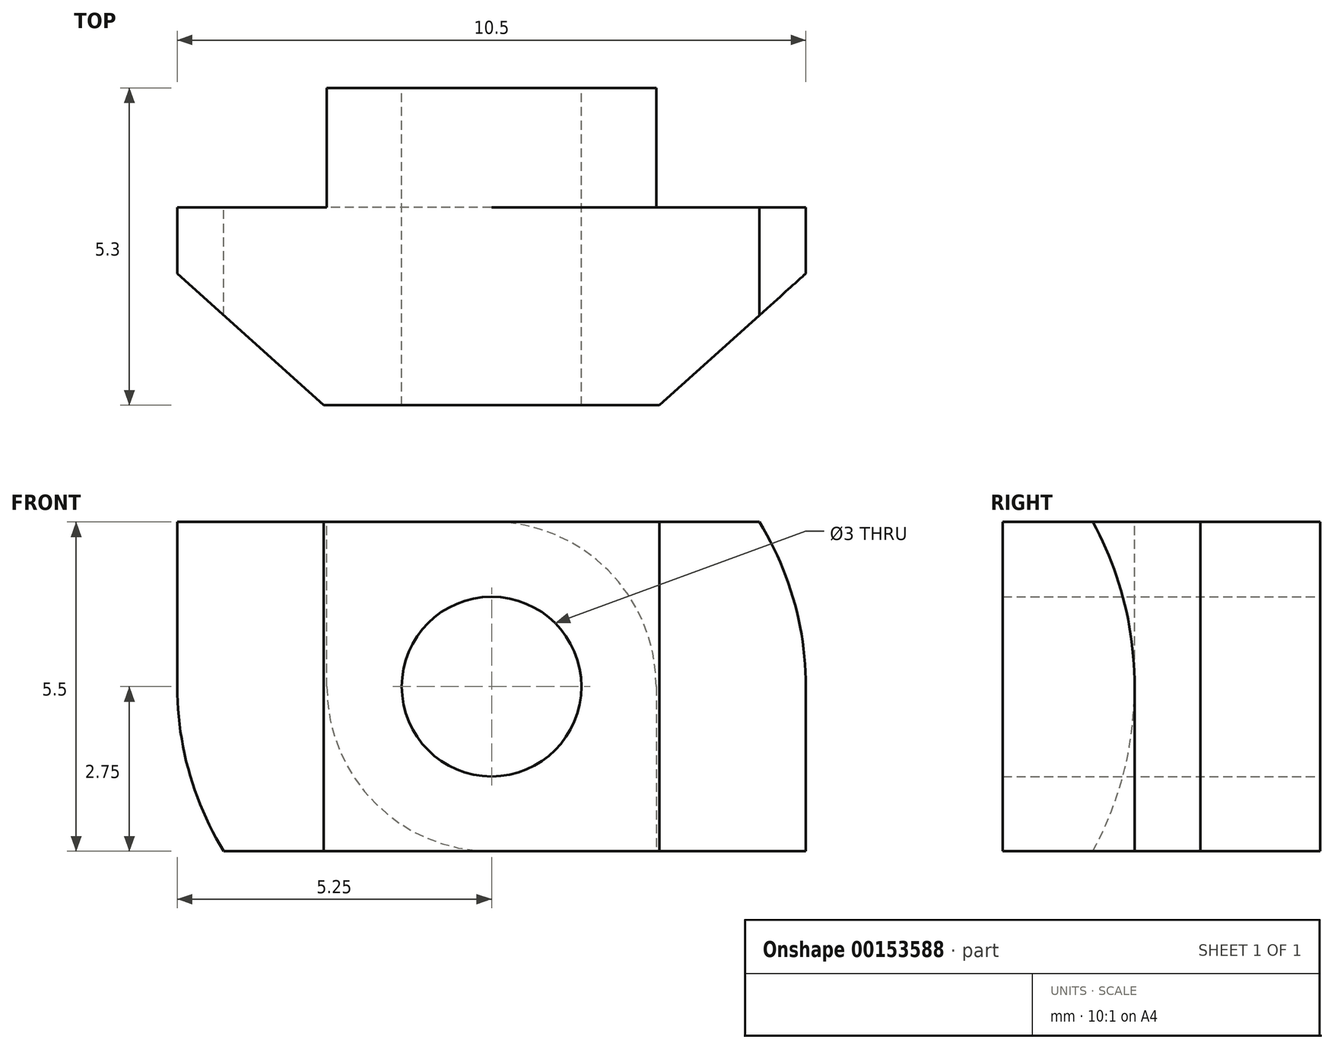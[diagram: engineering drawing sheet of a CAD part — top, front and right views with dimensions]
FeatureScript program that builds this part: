
annotation { "Feature Type Name" : "Feature", "Feature Type Description" : "" }
export const myFeature = defineFeature(function(context is Context, id is Id, definition is map)
    precondition{}
    {
        {
            var Q0;
            Q0=qCreatedBy(makeId("Front.planeOp"),FACE);
            var sketch = newSketch(context, id + "F0", { "sketchPlane" : qUnion([Q0])});
            skLineSegment(sketch, "E0.bottom", {"start": v(5.25, -2.75) * mm, "end": v(-5.25, -2.75) * mm});
            skLineSegment(sketch, "E0.top", {"start": v(5.25, 2.75) * mm, "end": v(-5.25, 2.75) * mm});
            skLineSegment(sketch, "E0.left", {"start": v(5.25, -2.75) * mm, "end": v(5.25, 2.75) * mm});
            skLineSegment(sketch, "E0.right", {"start": v(-5.25, -2.75) * mm, "end": v(-5.25, 2.75) * mm});
            skPoint(sketch, "E0.middle", {"position": v(0, 0) * mm});
            skCircle(sketch, "E1", {"center": v(0, 0) * mm, "radius": 5.25 * mm});
            skCircle(sketch, "E2", {"center": v(0, 0) * mm, "radius": 1.5 * mm});
            skSolve(sketch);
        }
        {
            var Q0;
            Q0=makeQuery(id+"F0.imprint","IMPRINT",FACE,{"disambiguationData":[TD([[makeQuery(id+"F0.imprint","IMPRINT",EDGE,{"derivedFrom":sQuery(id+"F0.wireOp",EDGE,"E2")}),-1.0]])]});
            var Q1;
            {var subQ0=sQuery(id+"F0.wireOp",EDGE,"E0.right");var subQ1=sQuery(id+"F0.wireOp",EDGE,"E0.top");var subQ2=makeQuery(id+"F0.imprint","INTERSECT",VERTEX,{"derivedFrom":[subQ1,subQ0]});Q1=makeQuery(id+"F0.imprint","IMPRINT",FACE,{"disambiguationData":[TD([[makeQuery(id+"F0.imprint","IMPRINT",EDGE,{"disambiguationData":[TD([[subQ2,1.0]])],"derivedFrom":subQ1}),1.0]])]});}
            var Q2;
            {var subQ0=sQuery(id+"F0.wireOp",EDGE,"E0.left");var subQ1=sQuery(id+"F0.wireOp",EDGE,"E0.bottom");var subQ2=makeQuery(id+"F0.imprint","INTERSECT",VERTEX,{"derivedFrom":[subQ1,subQ0]});Q2=makeQuery(id+"F0.imprint","IMPRINT",FACE,{"disambiguationData":[TD([[makeQuery(id+"F0.imprint","IMPRINT",EDGE,{"disambiguationData":[TD([[subQ2,-1.0]])],"derivedFrom":subQ1}),-1.0]])]});}
            extrude(context, id + "F1", {"entities" : qUnion([Q0, Q1, Q2]), "depth" : 3.8 * mm});
        }
        {
            var Q0;
            Q0=makeQuery(id+"F1.opExtrude","CAP_FACE",FACE,{"disambiguationData":[OSD([sQuery(id+"F0.wireOp",EDGE,"E0.bottom"),sQuery(id+"F0.wireOp",EDGE,"E0.top"),sQuery(id+"F0.wireOp",EDGE,"E0.left"),sQuery(id+"F0.wireOp",EDGE,"E0.right"),sQuery(id+"F0.wireOp",EDGE,"E1"),sQuery(id+"F0.wireOp",EDGE,"E2")])],"isStart":true});
            var sketch = newSketch(context, id + "F2", { "sketchPlane" : qUnion([Q0])});
            skCircle(sketch, "E3", {"center": v(0, 0) * mm, "radius": 2.75 * mm});
            skLineSegment(sketch, "E4", {"start": v(2.75, 0) * mm, "end": v(2.75, -2.75) * mm});
            skLineSegment(sketch, "E5", {"start": v(0, -2.75) * mm, "end": v(2.75, -2.75) * mm});
            skLineSegment(sketch, "E6", {"start": v(-2.75, 0) * mm, "end": v(-2.75, 2.75) * mm});
            skLineSegment(sketch, "E7", {"start": v(-2.75, 2.75) * mm, "end": v(0, 2.75) * mm});
            skCircle(sketch, "E8", {"center": v(0, 0) * mm, "radius": 1.5 * mm});
            skLineSegment(sketch, "E9", {"start": v(2.75, 0) * mm, "end": v(-2.75, 0) * mm});
            skLineSegment(sketch, "E10.MirrorCS", {"start": v(-2.75, 0) * mm, "end": v(-2.75, -2.75) * mm});
            skLineSegment(sketch, "E11.MirrorCS", {"start": v(-2.75, -2.75) * mm, "end": v(0, -2.75) * mm});
            skLineSegment(sketch, "E12.MirrorCS", {"start": v(2.75, 0) * mm, "end": v(2.75, 2.75) * mm});
            skLineSegment(sketch, "E13.MirrorCS", {"start": v(0, 2.75) * mm, "end": v(2.75, 2.75) * mm});
            skSolve(sketch);
        }
        {
            var Q0;
            {var subQ2=sQuery(id+"F2.wireOp",EDGE,"E10.MirrorCS");Q0=makeQuery(id+"F2.imprint","IMPRINT",FACE,{"disambiguationData":[TD([[makeQuery(id+"F2.imprint","IMPRINT",EDGE,{"derivedFrom":subQ2}),1.0]])]});}
            var Q1;
            {var subQ0=sQuery(id+"F2.wireOp",EDGE,"E9");var subQ3=sQuery(id+"F2.wireOp",EDGE,"E8");var subQ4=makeQuery(id+"F2.imprint","INTERSECT",VERTEX,{"disambiguationData":[OD(0.0)],"derivedFrom":[subQ3,subQ0]});Q1=makeQuery(id+"F2.imprint","IMPRINT",FACE,{"disambiguationData":[TD([[makeQuery(id+"F2.imprint","IMPRINT",EDGE,{"disambiguationData":[TD([[subQ4,1.0]])],"derivedFrom":subQ3}),1.0]])]});}
            var Q2;
            {var subQ0=sQuery(id+"F2.wireOp",EDGE,"E9");var subQ3=sQuery(id+"F2.wireOp",EDGE,"E8");var subQ4=makeQuery(id+"F2.imprint","INTERSECT",VERTEX,{"disambiguationData":[OD(0.0)],"derivedFrom":[subQ3,subQ0]});Q2=makeQuery(id+"F2.imprint","IMPRINT",FACE,{"disambiguationData":[TD([[makeQuery(id+"F2.imprint","IMPRINT",EDGE,{"disambiguationData":[TD([[subQ4,-1.0]])],"derivedFrom":subQ3}),1.0]])]});}
            var Q3;
            {var subQ0=sQuery(id+"F2.wireOp",EDGE,"E12.MirrorCS");Q3=makeQuery(id+"F2.imprint","IMPRINT",FACE,{"disambiguationData":[TD([[makeQuery(id+"F2.imprint","IMPRINT",EDGE,{"derivedFrom":subQ0}),1.0]])]});}
            extrude(context, id + "F3", {"entities" : qUnion([Q0, Q1, Q2, Q3]), "operationType" : NewBodyOperationType.ADD, "depth" : 2 * mm});
        }
        {
            var Q0;
            Q0=makeQuery(id+"F3.boolean.opBoolean","MERGE",FACE,{"derivedFrom":[makeQuery(id+"F1.opExtrude","SWEPT_FACE",FACE,{"disambiguationData":[OSD([sQuery(id+"F0.wireOp",EDGE,"E0.top")])]}),makeQuery(id+"F3.opExtrude","SWEPT_FACE",FACE,{"disambiguationData":[OSD([sQuery(id+"F2.wireOp",EDGE,"E7")])]})]});
            var sketch = newSketch(context, id + "F4", { "sketchPlane" : qUnion([Q0])});
            skLineSegment(sketch, "E14", {"start": v(-5.25, -3.8) * mm, "end": v(-2.25, -3.8) * mm});
            skLineSegment(sketch, "E15", {"start": v(5.25, -3.8) * mm, "end": v(2.25, -3.8) * mm});
            skLineSegment(sketch, "E16", {"start": v(-5.25, -3.8) * mm, "end": v(-5.25, -1.1) * mm});
            skLineSegment(sketch, "E17", {"start": v(2.25, -3.8) * mm, "end": v(5.25, -1.1) * mm});
            skLineSegment(sketch, "E18", {"start": v(-2.25, -3.8) * mm, "end": v(-5.25, -1.1) * mm});
            skLineSegment(sketch, "E19", {"start": v(5.25, -3.8) * mm, "end": v(5.25, -1.1) * mm});
            skSolve(sketch);
        }
        {
            var Q0;
            Q0 = qSketchRegion(id + "F4", true);
            extrude(context, id + "F5", {"entities" : qUnion([Q0]), "operationType" : NewBodyOperationType.REMOVE, "oppositeDirection" : true, "depth" : 25 * mm});
        }
        {
            var Q0;
            Q0=makeQuery(id+"F3.boolean.opBoolean","MERGE",FACE,{"derivedFrom":[makeQuery(id+"F1.opExtrude","SWEPT_FACE",FACE,{"disambiguationData":[OSD([sQuery(id+"F0.wireOp",EDGE,"E0.top")])]}),makeQuery(id+"F3.opExtrude","SWEPT_FACE",FACE,{"disambiguationData":[OSD([sQuery(id+"F2.wireOp",EDGE,"E13.MirrorCS")])]})]});
            var sketch = newSketch(context, id + "F6", { "sketchPlane" : qUnion([Q0])});
            skLineSegment(sketch, "E20.bottom", {"start": v(-3.05, -3.8) * mm, "end": v(2.92, -3.8) * mm});
            skLineSegment(sketch, "E20.top", {"start": v(-3.05, -3.3) * mm, "end": v(2.92, -3.3) * mm});
            skLineSegment(sketch, "E20.left", {"start": v(-3.05, -3.8) * mm, "end": v(-3.05, -3.3) * mm});
            skLineSegment(sketch, "E20.right", {"start": v(2.92, -3.8) * mm, "end": v(2.92, -3.3) * mm});
            skSolve(sketch);
        }
        {
            var Q0;
            Q0 = qSketchRegion(id + "F6", true);
            extrude(context, id + "F7", {"entities" : qUnion([Q0]), "operationType" : NewBodyOperationType.REMOVE, "oppositeDirection" : true, "depth" : 25 * mm});
        }
    });
